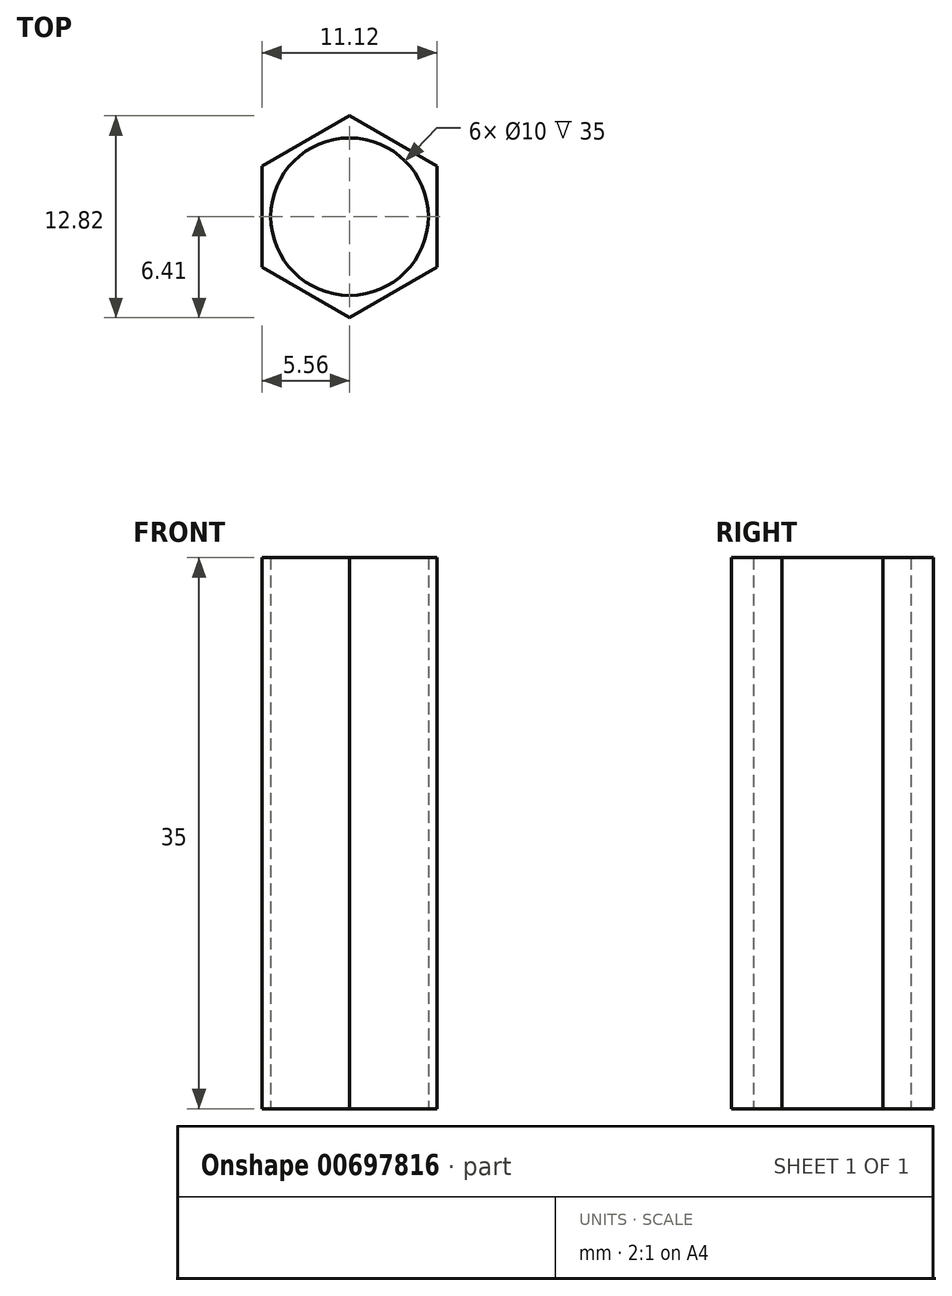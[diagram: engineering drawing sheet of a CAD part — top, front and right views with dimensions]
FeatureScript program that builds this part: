
annotation { "Feature Type Name" : "Feature", "Feature Type Description" : "" }
export const myFeature = defineFeature(function(context is Context, id is Id, definition is map)
    precondition{}
    {
        {
            var Q0;
            Q0=qCreatedBy(makeId("Top.planeOp"),FACE);
            var sketch = newSketch(context, id + "F0", { "sketchPlane" : qUnion([Q0])});
            skCircle(sketch, "E0.cCircle", {"center": v(0, 0) * mm, "radius": 5.56 * mm, "construction": true});
            skLineSegment(sketch, "E0.0", {"start": v(-5.56, -3.2) * mm, "end": v(-5.56, 3.2) * mm});
            skLineSegment(sketch, "E0.1", {"start": v(-5.56, 3.2) * mm, "end": v(0, 6.41) * mm});
            skLineSegment(sketch, "E0.2", {"start": v(0, 6.41) * mm, "end": v(5.55, 3.2) * mm});
            skLineSegment(sketch, "E0.3", {"start": v(5.55, 3.2) * mm, "end": v(5.56, -3.2) * mm});
            skLineSegment(sketch, "E0.4", {"start": v(5.56, -3.2) * mm, "end": v(0, -6.41) * mm});
            skLineSegment(sketch, "E0.5", {"start": v(0, -6.41) * mm, "end": v(-5.55, -3.2) * mm});
            skPoint(sketch, "E0.0.midPoint", {"position": v(-5.55, 0) * mm});
            skCircle(sketch, "E1", {"center": v(0, 0) * mm, "radius": 5 * mm});
            skSolve(sketch);
        }
        {
            var Q0;
            Q0=qSketchRegion(id+"F0",true);
            extrude(context, id + "F1", {"entities" : qUnion([Q0]), "depth" : 35 * mm, "offsetDistance" : 25 * mm});
        }
    });
